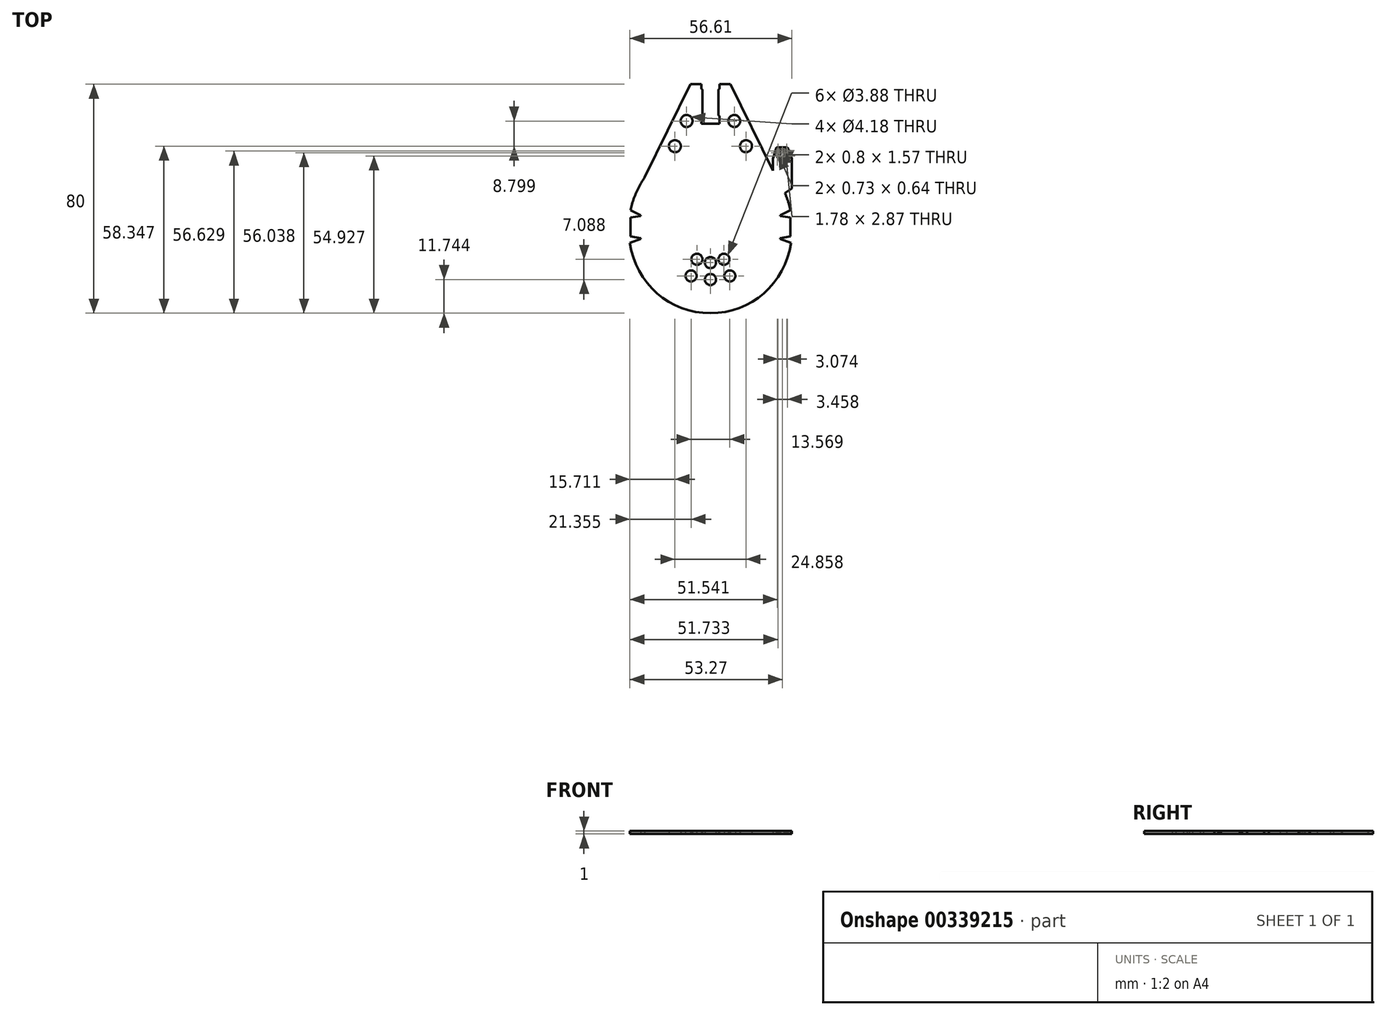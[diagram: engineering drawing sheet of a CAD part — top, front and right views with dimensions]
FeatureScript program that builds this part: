
annotation { "Feature Type Name" : "Feature", "Feature Type Description" : "" }
export const myFeature = defineFeature(function(context is Context, id is Id, definition is map)
    precondition{}
    {
        {
            var Q0;
            Q0=qCreatedBy(makeId("Top.planeOp"),FACE);
            var sketch = newSketch(context, id + "F0", { "sketchPlane" : qUnion([Q0])});
            skLineSegment(sketch, "E0", {"start": v(0, 26.26) * mm, "end": v(-3.12, 26.26) * mm});
            skLineSegment(sketch, "E1", {"start": v(-3.12, 26.26) * mm, "end": v(-3.12, 40.02) * mm});
            skLineSegment(sketch, "E2", {"start": v(-3.12, 40.02) * mm, "end": v(-7.04, 40.02) * mm});
            skLineSegment(sketch, "E3", {"start": v(-7.04, 40.02) * mm, "end": v(-22.96, 7.55) * mm});
            skFitSpline(sketch, "E4", {"points": [v(-22.96, 7.55) * mm, v(-27.98, -4.04) * mm], "startDerivative": vector(-7.07, -10.29) * mm, "endDerivative": vector(-2.64, -12.33) * mm});
            skLineSegment(sketch, "E5", {"start": v(-27.98, -4.04) * mm, "end": v(-24.34, -5.77) * mm});
            skLineSegment(sketch, "E6", {"start": v(-24.34, -5.77) * mm, "end": v(-24.34, -6.01) * mm});
            skLineSegment(sketch, "E7", {"start": v(-24.34, -6.01) * mm, "end": v(-27.98, -6.5) * mm});
            skLineSegment(sketch, "E8", {"start": v(-27.98, -6.5) * mm, "end": v(-27.98, -13.17) * mm});
            skLineSegment(sketch, "E9", {"start": v(-27.98, -13.17) * mm, "end": v(-24.34, -13.83) * mm});
            skLineSegment(sketch, "E10", {"start": v(-24.34, -13.83) * mm, "end": v(-24.34, -14.08) * mm});
            skLineSegment(sketch, "E11", {"start": v(-24.34, -14.08) * mm, "end": v(-28.14, -15.46) * mm});
            skArc(sketch, "E12", {"start": v(-28.14, -15.46) * mm, "mid": v(-0.14, -39.98) * mm, "end": v(27.85, -15.46) * mm});
            skLineSegment(sketch, "E13.MirrorCS", {"start": v(24.34, -13.83) * mm, "end": v(24.34, -14.08) * mm});
            skLineSegment(sketch, "E14.MirrorCS", {"start": v(24.34, -5.77) * mm, "end": v(24.34, -6.01) * mm});
            skLineSegment(sketch, "E15.MirrorCS", {"start": v(27.98, -4.04) * mm, "end": v(24.34, -5.77) * mm});
            skLineSegment(sketch, "E16.MirrorCS", {"start": v(24.34, -14.08) * mm, "end": v(28.14, -15.46) * mm});
            skLineSegment(sketch, "E17.MirrorCS", {"start": v(27.98, -13.17) * mm, "end": v(24.34, -13.83) * mm});
            skLineSegment(sketch, "E18.MirrorCS", {"start": v(3.12, 40.02) * mm, "end": v(7.04, 40.02) * mm});
            skLineSegment(sketch, "E19.MirrorCS", {"start": v(24.34, -6.01) * mm, "end": v(27.98, -6.5) * mm});
            skFitSpline(sketch, "E20.MirrorCS", {"points": [v(22.96, 7.55) * mm, v(27.98, -4.04) * mm], "startDerivative": vector(7.07, -10.29) * mm, "endDerivative": vector(2.64, -12.33) * mm});
            skLineSegment(sketch, "E21.MirrorCS", {"start": v(0, 26.26) * mm, "end": v(3.12, 26.26) * mm});
            skArc(sketch, "E22.MirrorCS", {"start": v(28.14, -15.46) * mm, "mid": v(0.14, -39.98) * mm, "end": v(-27.85, -15.46) * mm});
            skLineSegment(sketch, "E23.MirrorCS", {"start": v(27.98, -6.5) * mm, "end": v(27.98, -13.17) * mm});
            skLineSegment(sketch, "E24.MirrorCS", {"start": v(7.04, 40.02) * mm, "end": v(22.96, 7.55) * mm});
            skLineSegment(sketch, "E25.MirrorCS", {"start": v(3.12, 26.26) * mm, "end": v(3.12, 40.02) * mm});
            skLineSegment(sketch, "E26", {"start": v(21.82, 9.87) * mm, "end": v(21.82, 14) * mm});
            skLineSegment(sketch, "E27", {"start": v(21.82, 14) * mm, "end": v(23.16, 17.95) * mm});
            skLineSegment(sketch, "E28", {"start": v(23.16, 17.95) * mm, "end": v(27.14, 17.95) * mm});
            skLineSegment(sketch, "E29", {"start": v(26.98, 17.95) * mm, "end": v(28.47, 14) * mm});
            skLineSegment(sketch, "E30", {"start": v(28.47, 14) * mm, "end": v(28.47, 3.6) * mm});
            skLineSegment(sketch, "E31", {"start": v(28.47, 3.6) * mm, "end": v(26.02, 2.01) * mm});
            skLineSegment(sketch, "E32", {"start": v(24.57, 17.5) * mm, "end": v(25.7, 17.5) * mm});
            skLineSegment(sketch, "E33", {"start": v(25.7, 17.5) * mm, "end": v(26.02, 14.63) * mm});
            skLineSegment(sketch, "E34", {"start": v(26.02, 14.63) * mm, "end": v(24.24, 14.63) * mm});
            skLineSegment(sketch, "E35", {"start": v(24.24, 14.63) * mm, "end": v(24.57, 17.5) * mm});
            skLineSegment(sketch, "E36", {"start": v(23.45, 17.43) * mm, "end": v(24, 17.43) * mm});
            skLineSegment(sketch, "E37", {"start": v(24, 17.43) * mm, "end": v(23.84, 15.86) * mm});
            skLineSegment(sketch, "E38", {"start": v(23.84, 15.86) * mm, "end": v(23.2, 15.86) * mm});
            skLineSegment(sketch, "E39", {"start": v(23.2, 15.86) * mm, "end": v(23.45, 17.43) * mm});
            skLineSegment(sketch, "E40", {"start": v(23.1, 15.27) * mm, "end": v(23.77, 15.27) * mm});
            skLineSegment(sketch, "E41", {"start": v(23.77, 15.27) * mm, "end": v(23.7, 14.63) * mm});
            skLineSegment(sketch, "E42", {"start": v(23.7, 14.63) * mm, "end": v(23.03, 14.63) * mm});
            skLineSegment(sketch, "E43", {"start": v(23.03, 14.63) * mm, "end": v(23.1, 15.27) * mm});
            skLineSegment(sketch, "E44.MirrorCS", {"start": v(26.42, 15.86) * mm, "end": v(27.07, 15.86) * mm});
            skLineSegment(sketch, "E45.MirrorCS", {"start": v(26.26, 17.43) * mm, "end": v(26.42, 15.86) * mm});
            skLineSegment(sketch, "E46.MirrorCS", {"start": v(26.57, 14.63) * mm, "end": v(27.22, 14.63) * mm});
            skLineSegment(sketch, "E47.MirrorCS", {"start": v(26.8, 17.43) * mm, "end": v(26.26, 17.43) * mm});
            skLineSegment(sketch, "E48.MirrorCS", {"start": v(27.16, 15.27) * mm, "end": v(26.5, 15.27) * mm});
            skLineSegment(sketch, "E49.MirrorCS", {"start": v(26.5, 15.27) * mm, "end": v(26.57, 14.63) * mm});
            skLineSegment(sketch, "E50.MirrorCS", {"start": v(27.07, 15.86) * mm, "end": v(26.8, 17.43) * mm});
            skLineSegment(sketch, "E51.MirrorCS", {"start": v(27.22, 14.63) * mm, "end": v(27.16, 15.27) * mm});
            skCircle(sketch, "E52", {"center": v(-8.34, 27.17) * mm, "radius": 2.1 * mm});
            skCircle(sketch, "E53", {"center": v(-12.43, 18.37) * mm, "radius": 2.1 * mm});
            skCircle(sketch, "E54.MirrorC", {"center": v(8.34, 27.17) * mm, "radius": 2.1 * mm});
            skCircle(sketch, "E55.MirrorC", {"center": v(12.43, 18.37) * mm, "radius": 2.1 * mm});
            skCircle(sketch, "E56", {"center": v(-4.73, -21.15) * mm, "radius": 1.94 * mm});
            skCircle(sketch, "E57", {"center": v(-6.78, -26.97) * mm, "radius": 1.94 * mm});
            skCircle(sketch, "E58.MirrorC", {"center": v(4.73, -21.15) * mm, "radius": 1.94 * mm});
            skCircle(sketch, "E59.MirrorC", {"center": v(6.78, -26.97) * mm, "radius": 1.94 * mm});
            skCircle(sketch, "E60", {"center": v(0, -22.31) * mm, "radius": 1.94 * mm});
            skCircle(sketch, "E61", {"center": v(0, -28.24) * mm, "radius": 1.94 * mm});
            skLineSegment(sketch, "E62", {"start": v(-3.12, 38.44) * mm, "end": v(-2.8, 38.16) * mm});
            skLineSegment(sketch, "E63", {"start": v(-2.8, 38.16) * mm, "end": v(-2.8, 29.11) * mm});
            skLineSegment(sketch, "E64", {"start": v(-2.8, 29.11) * mm, "end": v(-3.12, 28.83) * mm});
            skLineSegment(sketch, "E65.MirrorCS", {"start": v(2.8, 38.16) * mm, "end": v(2.8, 29.11) * mm});
            skLineSegment(sketch, "E66.MirrorCS", {"start": v(3.12, 38.44) * mm, "end": v(2.8, 38.16) * mm});
            skLineSegment(sketch, "E67.MirrorCS", {"start": v(2.8, 29.11) * mm, "end": v(3.12, 28.83) * mm});
            skLineSegment(sketch, "E68", {"start": v(-3.12, 40.02) * mm, "end": v(3.12, 40.02) * mm, "construction": true});
            skLineSegment(sketch, "E69", {"start": v(0, 40.02) * mm, "end": v(0, -39.98) * mm, "construction": true});
            skLineSegment(sketch, "E70", {"start": v(-0.02, -39.98) * mm, "end": v(73.76, -40.6) * mm});
            skSolve(sketch);
        }
        {
            var Q0;
            Q0=makeQuery(id+"F0.imprint","IMPRINT",FACE,{"disambiguationData":[TD([[makeQuery(id+"F0.imprint","IMPRINT",EDGE,{"derivedFrom":sQuery(id+"F0.wireOp",EDGE,"E0")}),1.0]])]});
            var Q1;
            {var subQ1=sQuery(id+"F0.wireOp",EDGE,"E26");Q1=makeQuery(id+"F0.imprint","IMPRINT",FACE,{"disambiguationData":[TD([[makeQuery(id+"F0.imprint","IMPRINT",EDGE,{"derivedFrom":subQ1}),-1.0]])]});}
            var Q2;
            {var subQ0=sQuery(id+"F0.wireOp",EDGE,"tkkGbWxD-1snL-wY6W-PjNo-pDHXJ1ULXX12");Q2=makeQuery(id+"F0.imprint","IMPRINT",FACE,{"disambiguationData":[TD([[makeQuery(id+"F0.imprint","IMPRINT",EDGE,{"derivedFrom":subQ0}),-1.0]])]});}
            var Q3;
            {var subQ0=sQuery(id+"F0.wireOp",EDGE,"428d8ecf-713a-43c6-a231-88eb7b8979cb0.MirrorCS");Q3=makeQuery(id+"F0.imprint","IMPRINT",FACE,{"disambiguationData":[TD([[makeQuery(id+"F0.imprint","IMPRINT",EDGE,{"derivedFrom":subQ0}),1.0]])]});}
            var Q4;
            {var subQ0=sQuery(id+"F0.wireOp",EDGE,"E62");Q4=makeQuery(id+"F0.imprint","IMPRINT",FACE,{"disambiguationData":[TD([[makeQuery(id+"F0.imprint","IMPRINT",EDGE,{"derivedFrom":subQ0}),-1.0]])]});}
            var Q5;
            Q5=makeQuery(id+"F0.imprint","IMPRINT",FACE,{"disambiguationData":[TD([[makeQuery(id+"F0.imprint","IMPRINT",EDGE,{"derivedFrom":sQuery(id+"F0.wireOp",EDGE,"E65.MirrorCS")}),1.0]])]});
            extrude(context, id + "F1", {"entities" : qUnion([Q0, Q1, Q2, Q3, Q4, Q5]), "depth" : 1 * mm});
        }
    });
